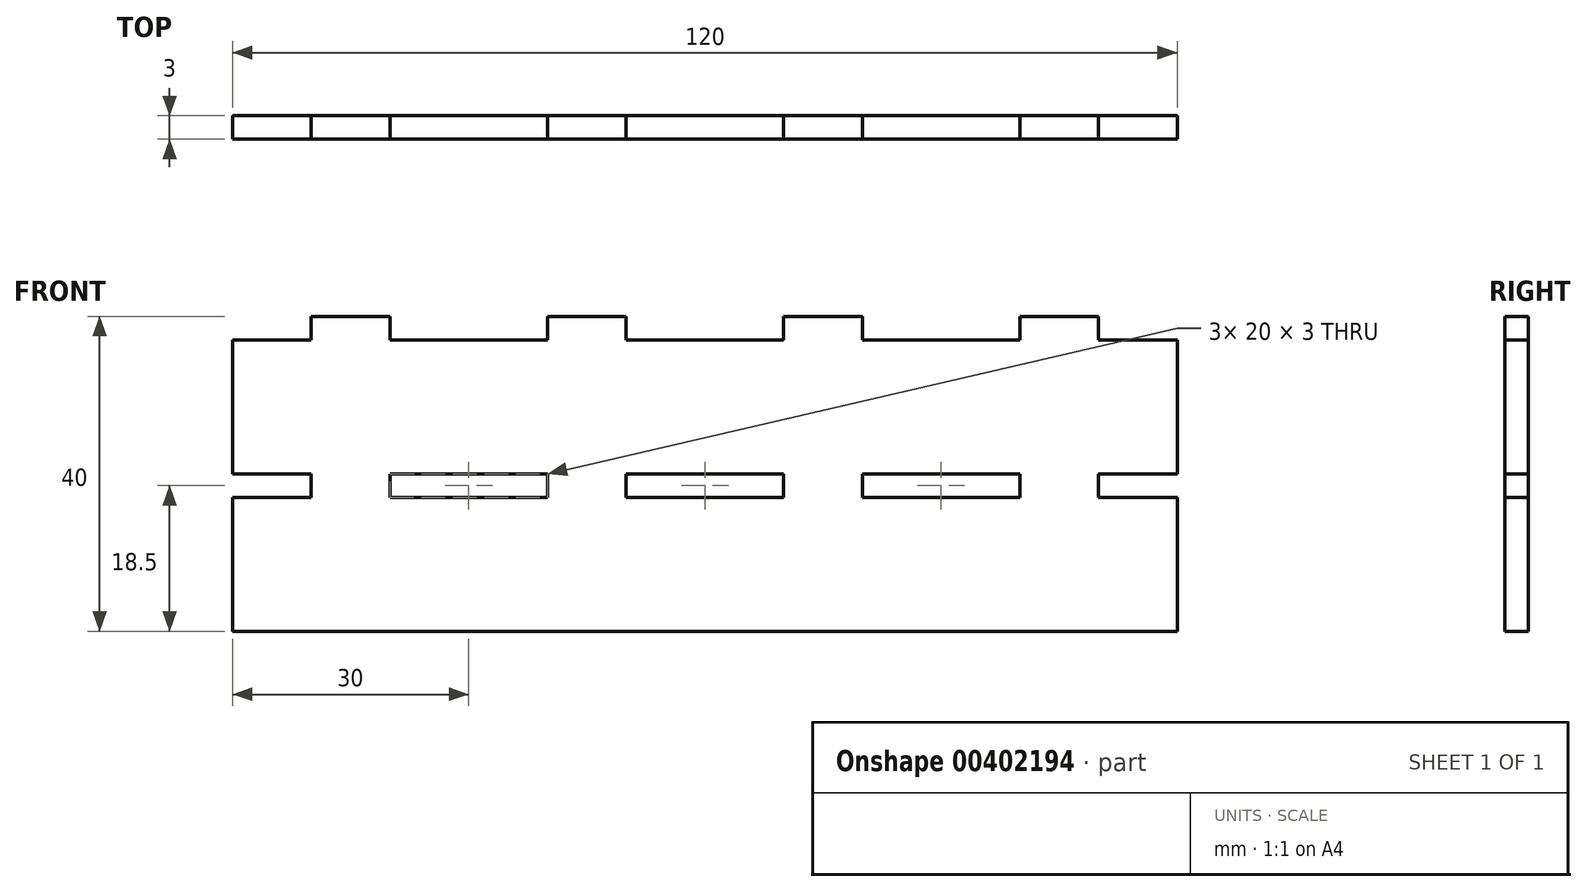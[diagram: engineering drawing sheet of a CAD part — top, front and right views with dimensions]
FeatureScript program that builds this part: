
annotation { "Feature Type Name" : "Feature", "Feature Type Description" : "" }
export const myFeature = defineFeature(function(context is Context, id is Id, definition is map)
    precondition{}
    {
        {
            assignVariable(context, id + "F0", {"name" : "t", "anyValue" : 3});
        }
        {
            var Q0;
            Q0=qCreatedBy(makeId("Front.planeOp"),FACE);
            var sketch = newSketch(context, id + "F1", { "sketchPlane" : qUnion([Q0])});
            skLineSegment(sketch, "E0.bottom", {"start": v(60, -20) * mm, "end": v(-60, -20) * mm});
            skLineSegment(sketch, "E0.top", {"start": v(60, 20) * mm, "end": v(-60, 20) * mm});
            skLineSegment(sketch, "E0.left", {"start": v(60, -20) * mm, "end": v(60, 20) * mm});
            skLineSegment(sketch, "E0.right", {"start": v(-60, -20) * mm, "end": v(-60, 20) * mm});
            skPoint(sketch, "E0.middle", {"position": v(0, 0) * mm});
            skLineSegment(sketch, "E1.bottom", {"start": v(-60, 20) * mm, "end": v(-50, 20) * mm});
            skLineSegment(sketch, "E1.top", {"start": v(-60, 17) * mm, "end": v(-50, 17) * mm});
            skLineSegment(sketch, "E1.left", {"start": v(-60, 20) * mm, "end": v(-60, 17) * mm});
            skLineSegment(sketch, "E1.right", {"start": v(-50, 20) * mm, "end": v(-50, 17) * mm});
            skLineSegment(sketch, "E2.MirrorCS", {"start": v(50, 20) * mm, "end": v(50, 17) * mm});
            skLineSegment(sketch, "E3.MirrorCS", {"start": v(60, 20) * mm, "end": v(50, 20) * mm});
            skLineSegment(sketch, "E4.MirrorCS", {"start": v(60, 20) * mm, "end": v(60, 17) * mm});
            skLineSegment(sketch, "E5.MirrorCS", {"start": v(60, 17) * mm, "end": v(50, 17) * mm});
            skLineSegment(sketch, "E6.bottom", {"start": v(-40, 20) * mm, "end": v(-20, 20) * mm});
            skLineSegment(sketch, "E6.top", {"start": v(-40, 17) * mm, "end": v(-20, 17) * mm});
            skLineSegment(sketch, "E6.left", {"start": v(-40, 20) * mm, "end": v(-40, 17) * mm});
            skLineSegment(sketch, "E6.right", {"start": v(-20, 20) * mm, "end": v(-20, 17) * mm});
            skLineSegment(sketch, "E7.1.0.0", {"start": v(-10, 20) * mm, "end": v(10, 20) * mm});
            skLineSegment(sketch, "E7.1.0.1", {"start": v(-10, 17) * mm, "end": v(10, 17) * mm});
            skLineSegment(sketch, "E7.1.0.2", {"start": v(-10, 20) * mm, "end": v(-10, 17) * mm});
            skLineSegment(sketch, "E7.1.0.3", {"start": v(10, 20) * mm, "end": v(10, 17) * mm});
            skLineSegment(sketch, "E7.2.0.0", {"start": v(20, 20) * mm, "end": v(40, 20) * mm});
            skLineSegment(sketch, "E7.2.0.1", {"start": v(20, 17) * mm, "end": v(40, 17) * mm});
            skLineSegment(sketch, "E7.2.0.2", {"start": v(20, 20) * mm, "end": v(20, 17) * mm});
            skLineSegment(sketch, "E7.2.0.3", {"start": v(40, 20) * mm, "end": v(40, 17) * mm});
            skLineSegment(sketch, "E7.direction1", {"start": v(-40, 17) * mm, "end": v(-10, 17) * mm, "construction": true});
            skLineSegment(sketch, "E8", {"start": v(60, 0) * mm, "end": v(-60, 0) * mm, "construction": true});
            skLineSegment(sketch, "E9.0.1.0", {"start": v(-60, 0) * mm, "end": v(-60, -3) * mm});
            skLineSegment(sketch, "E9.0.1.1", {"start": v(-60, 0) * mm, "end": v(-50, 0) * mm});
            skLineSegment(sketch, "E9.0.1.2", {"start": v(-60, -3) * mm, "end": v(-50, -3) * mm});
            skLineSegment(sketch, "E9.0.1.3", {"start": v(-50, 0) * mm, "end": v(-50, -3) * mm});
            skLineSegment(sketch, "E9.0.1.4", {"start": v(-50, 0) * mm, "end": v(-50, -3) * mm});
            skLineSegment(sketch, "E9.0.1.5", {"start": v(-60, -3) * mm, "end": v(-50, -3) * mm});
            skLineSegment(sketch, "E9.0.1.6", {"start": v(-60, 0) * mm, "end": v(-60, -3) * mm});
            skLineSegment(sketch, "E9.0.1.7", {"start": v(-40, 0) * mm, "end": v(-20, 0) * mm});
            skLineSegment(sketch, "E9.0.1.8", {"start": v(-40, 0) * mm, "end": v(-40, -3) * mm});
            skLineSegment(sketch, "E9.0.1.9", {"start": v(-40, -3) * mm, "end": v(-20, -3) * mm});
            skLineSegment(sketch, "E9.0.1.10", {"start": v(-20, 0) * mm, "end": v(-20, -3) * mm});
            skLineSegment(sketch, "E9.0.1.11", {"start": v(10, 0) * mm, "end": v(10, -3) * mm});
            skLineSegment(sketch, "E9.0.1.12", {"start": v(-10, 0) * mm, "end": v(10, 0) * mm});
            skLineSegment(sketch, "E9.0.1.13", {"start": v(-10, 0) * mm, "end": v(-10, -3) * mm});
            skLineSegment(sketch, "E9.0.1.14", {"start": v(-10, -3) * mm, "end": v(10, -3) * mm});
            skLineSegment(sketch, "E9.0.1.15", {"start": v(20, 0) * mm, "end": v(40, 0) * mm});
            skLineSegment(sketch, "E9.0.1.16", {"start": v(20, -3) * mm, "end": v(40, -3) * mm});
            skLineSegment(sketch, "E9.0.1.17", {"start": v(20, 0) * mm, "end": v(20, -3) * mm});
            skLineSegment(sketch, "E9.0.1.18", {"start": v(40, 0) * mm, "end": v(40, -3) * mm});
            skLineSegment(sketch, "E9.0.1.19", {"start": v(60, 0) * mm, "end": v(50, 0) * mm});
            skLineSegment(sketch, "E9.0.1.20", {"start": v(60, 0) * mm, "end": v(60, -3) * mm});
            skLineSegment(sketch, "E9.0.1.21", {"start": v(50, 0) * mm, "end": v(50, -3) * mm});
            skLineSegment(sketch, "E9.0.1.22", {"start": v(60, -3) * mm, "end": v(50, -3) * mm});
            skLineSegment(sketch, "E9.0.1.23", {"start": v(60, -3) * mm, "end": v(50, -3) * mm});
            skLineSegment(sketch, "E9.0.1.24", {"start": v(60, 0) * mm, "end": v(60, -3) * mm});
            skLineSegment(sketch, "E9.0.1.25", {"start": v(60, 0) * mm, "end": v(50, 0) * mm});
            skLineSegment(sketch, "E9.0.1.26", {"start": v(50, 0) * mm, "end": v(50, -3) * mm});
            skLineSegment(sketch, "E9.direction1", {"start": v(-60, 17) * mm, "end": v(-35, 17) * mm, "construction": true});
            skLineSegment(sketch, "E9.direction2", {"start": v(-60, 17) * mm, "end": v(-60, -3) * mm, "construction": true});
            skSolve(sketch);
        }
        {
            var Q0;
            Q0=makeQuery(id+"F1.imprint","IMPRINT",FACE,{"disambiguationData":[TD([[makeQuery(id+"F1.imprint","IMPRINT",EDGE,{"derivedFrom":sQuery(id+"F1.wireOp",EDGE,"E0.bottom")}),-1.0]])]});
            extrude(context, id + "F2", {"entities" : qUnion([Q0]), "oppositeDirection" : true, "depth" : getVariable(context, 't') * mm});
        }
    });
